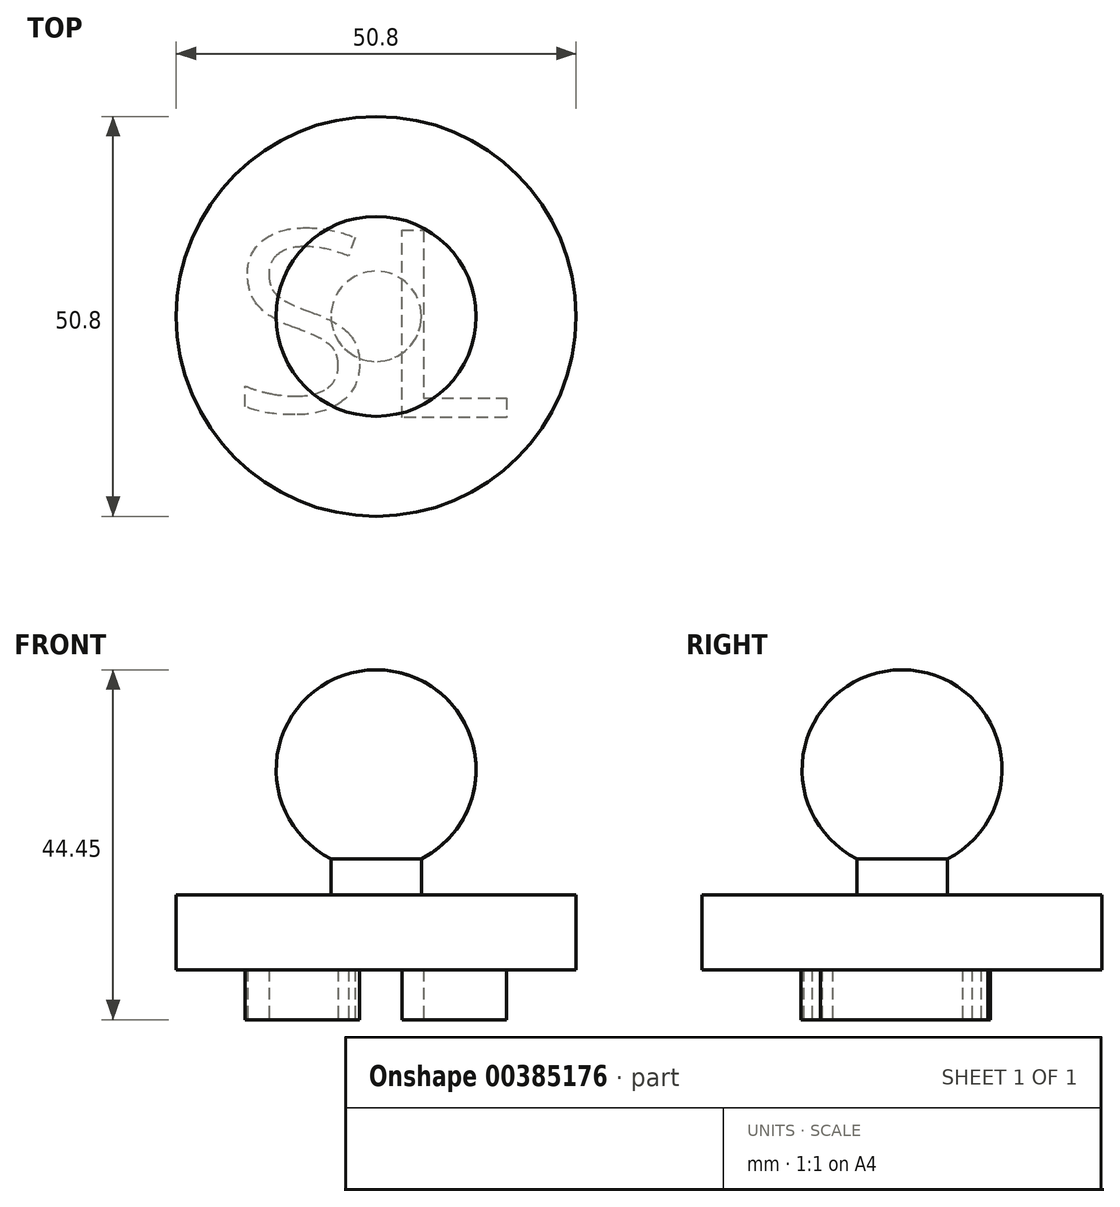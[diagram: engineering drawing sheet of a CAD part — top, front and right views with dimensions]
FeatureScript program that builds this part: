
annotation { "Feature Type Name" : "Feature", "Feature Type Description" : "" }
export const myFeature = defineFeature(function(context is Context, id is Id, definition is map)
    precondition{}
    {
        {
            var Q0;
            Q0=qCreatedBy(makeId("Front.planeOp"),FACE);
            var sketch = newSketch(context, id + "F0", { "sketchPlane" : qUnion([Q0])});
            skLineSegment(sketch, "E0", {"start": v(0, 0) * mm, "end": v(25.4, 0) * mm});
            skLineSegment(sketch, "E1", {"start": v(25.4, 0) * mm, "end": v(25.4, 9.52) * mm});
            skLineSegment(sketch, "E2", {"start": v(25.4, 9.53) * mm, "end": v(25.4, 9.53) * mm});
            skLineSegment(sketch, "E3", {"start": v(0, 38.1) * mm, "end": v(0, 0) * mm});
            skLineSegment(sketch, "E4", {"start": v(25.4, 9.53) * mm, "end": v(5.74, 9.52) * mm});
            skArc(sketch, "E5", {"start": v(0, 38.1) * mm, "mid": v(12.35, 28.35) * mm, "end": v(5.74, 14.07) * mm});
            skLineSegment(sketch, "E6", {"start": v(5.74, 14.07) * mm, "end": v(5.74, 9.52) * mm});
            skLineSegment(sketch, "E7", {"start": v(0, -6.35) * mm, "end": v(25.4, -6.35) * mm});
            skLineSegment(sketch, "E8", {"start": v(25.4, -6.35) * mm, "end": v(25.4, -19.05) * mm});
            skLineSegment(sketch, "E9", {"start": v(25.4, -19.05) * mm, "end": v(0, -19.05) * mm});
            skLineSegment(sketch, "E10", {"start": v(0, -19.05) * mm, "end": v(0, -6.35) * mm});
            skSolve(sketch);
        }
        {
            var Q0;
            Q0=makeQuery(id+"F0.imprint","IMPRINT",FACE,{"disambiguationData":[TD([[makeQuery(id+"F0.imprint","IMPRINT",EDGE,{"derivedFrom":sQuery(id+"F0.wireOp",EDGE,"E0")}),1.0]])]});
            var Q1;
            Q1=makeQuery(id+"F0.imprint","IMPRINT",FACE,{"disambiguationData":[TD([[makeQuery(id+"F0.imprint","IMPRINT",EDGE,{"derivedFrom":sQuery(id+"F0.wireOp",EDGE,"E7")}),-1.0]])]});
            var Q2;
            Q2=sQuery(id+"F0.wireOp",EDGE,"E10");
            revolve(context, id + "F1", {"entities" : qUnion([Q0, Q1]), "axis" : qUnion([Q2]), "revolveType" : RevolveType.FULL});
        }
        {
            var Q0;
            Q0=makeQuery(id+"F1.opRevolve","SWEPT_FACE",FACE,{"disambiguationData":[OSD([sQuery(id+"F0.wireOp",EDGE,"E7")])]});
            var sketch = newSketch(context, id + "F2", { "sketchPlane" : qUnion([Q0])});
            skText(sketch, "E11", { "text": "S", "fontName": "OpenSans-Regular.ttf"});
            skText(sketch, "E12", { "text": "L", "fontName": "OpenSans-Regular.ttf"});
            const initialGuessF2  = {"E11": [-0.01832, -0.01218, 1, 0, 0.0233], "E12": [0, -0.01287, 1, 0, 0.024]};
            skSetInitialGuess(sketch, initialGuessF2);
            skSolve(sketch);
        }
        {
            var Q0;
            Q0 = qSketchRegion(id + "F2", true);
            extrude(context, id + "F3", {"entities" : qUnion([Q0]), "operationType" : NewBodyOperationType.ADD, "depth" : 12.7 * mm});
        }
        {
            var Q0;
            Q0=makeQuery(id+"F1.opRevolve","SWEPT_FACE",FACE,{"disambiguationData":[OSD([sQuery(id+"F0.wireOp",EDGE,"E9")])]});
            var sketch = newSketch(context, id + "F4", { "sketchPlane" : qUnion([Q0])});
            skSolve(sketch);
        }
        {
            var Q0;
            Q0=makeQuery(id+"F4.imprint","IMPRINT",FACE,{"disambiguationData":[TD([[makeQuery(id+"F4.imprint","IMPRINT",EDGE,{"derivedFrom":makeQuery(id+"F1.opRevolve","SWEPT_EDGE",EDGE,{"disambiguationData":[OSD([sQuery(id+"F0.wireOp",EDGE,"E8"),sQuery(id+"F0.wireOp",EDGE,"E9")])]})}),1.0]])]});
            extrude(context, id + "F5", {"entities" : qUnion([Q0]), "operationType" : NewBodyOperationType.REMOVE, "oppositeDirection" : true, "depth" : 12.7 * mm});
        }
    });
